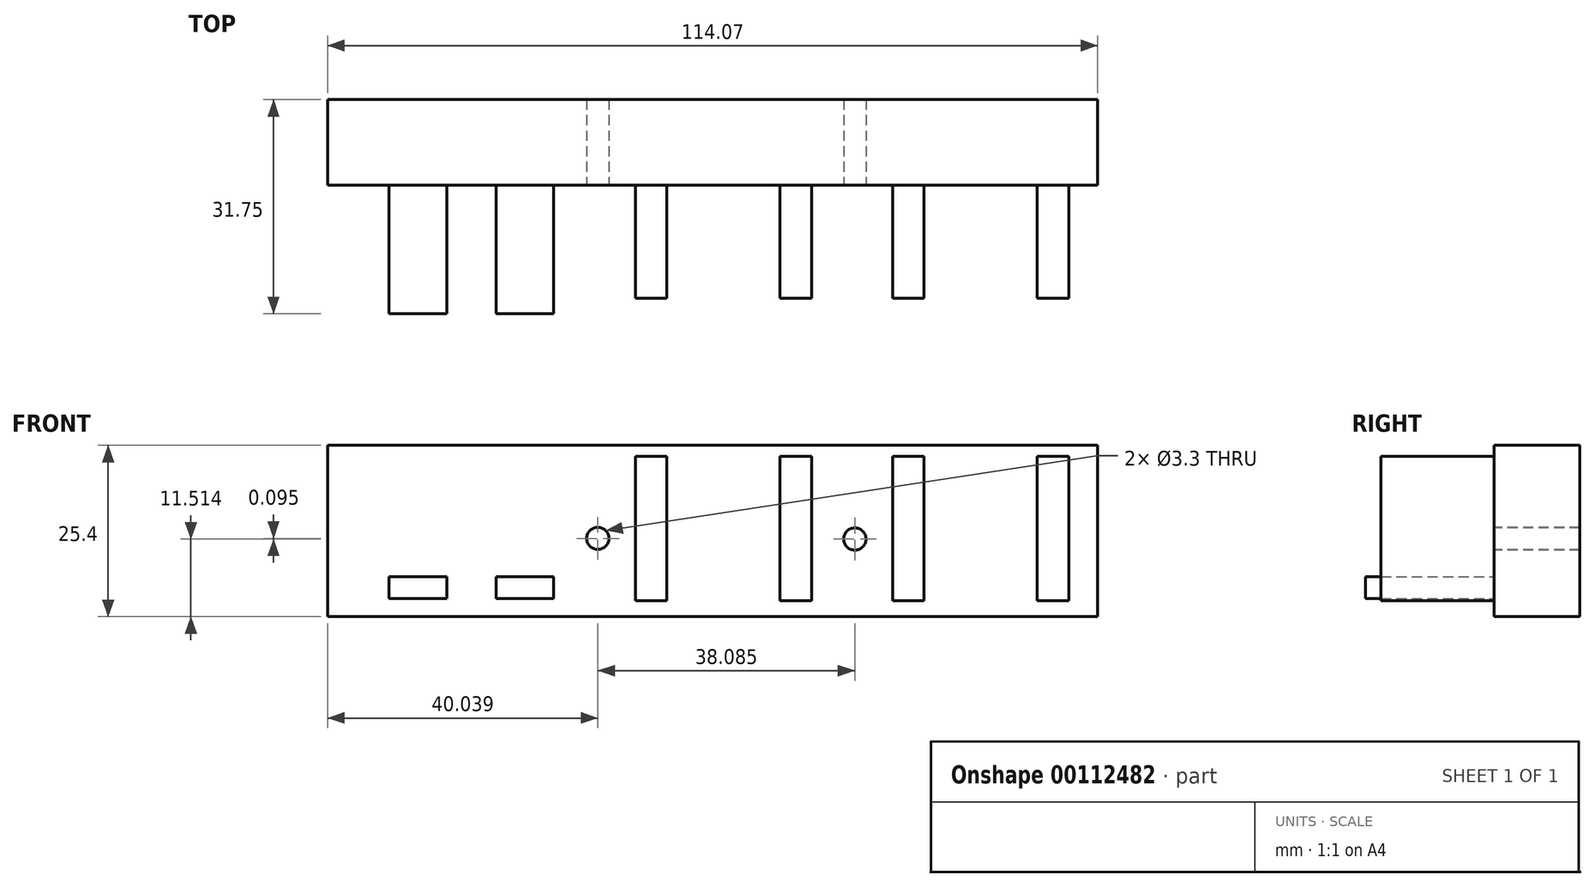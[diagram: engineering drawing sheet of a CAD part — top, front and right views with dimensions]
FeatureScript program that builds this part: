
annotation { "Feature Type Name" : "Feature", "Feature Type Description" : "" }
export const myFeature = defineFeature(function(context is Context, id is Id, definition is map)
    precondition{}
    {
        {
            var Q0;
            Q0=qCreatedBy(makeId("Front.planeOp"),FACE);
            var sketch = newSketch(context, id + "F0", { "sketchPlane" : qUnion([Q0])});
            skLineSegment(sketch, "E0", {"start": v(-72.64, 28.28) * mm, "end": v(54.36, 28.28) * mm});
            skLineSegment(sketch, "E1", {"start": v(54.36, 28.28) * mm, "end": v(54.36, 2.88) * mm});
            skLineSegment(sketch, "E2", {"start": v(54.36, 2.88) * mm, "end": v(-72.64, 2.88) * mm});
            skLineSegment(sketch, "E3", {"start": v(-72.64, 2.88) * mm, "end": v(-72.64, 28.28) * mm});
            skSolve(sketch);
        }
        {
            var Q0;
            Q0=makeQuery(id+"F0.imprint","IMPRINT",FACE,{"disambiguationData":[TD([[makeQuery(id+"F0.imprint","IMPRINT",EDGE,{"derivedFrom":sQuery(id+"F0.wireOp",EDGE,"E0")}),-1.0]])]});
            var sketch = newSketch(context, id + "F1", { "sketchPlane" : qUnion([Q0])});
            skLineSegment(sketch, "E4", {"start": v(50.08, 26.62) * mm, "end": v(50.08, 5.23) * mm});
            skLineSegment(sketch, "E5", {"start": v(50.08, 5.23) * mm, "end": v(45.41, 5.23) * mm});
            skLineSegment(sketch, "E6", {"start": v(45.41, 5.23) * mm, "end": v(45.41, 26.62) * mm});
            skLineSegment(sketch, "E7", {"start": v(45.41, 26.62) * mm, "end": v(50.08, 26.62) * mm});
            skLineSegment(sketch, "E8", {"start": v(45.41, 5.23) * mm, "end": v(28.65, 5.23) * mm, "construction": true});
            skLineSegment(sketch, "E9", {"start": v(28.65, 5.23) * mm, "end": v(28.65, 26.62) * mm});
            skLineSegment(sketch, "E10", {"start": v(28.65, 26.62) * mm, "end": v(23.98, 26.62) * mm});
            skLineSegment(sketch, "E11", {"start": v(23.98, 26.62) * mm, "end": v(23.98, 5.23) * mm});
            skLineSegment(sketch, "E12", {"start": v(23.98, 5.23) * mm, "end": v(28.65, 5.23) * mm});
            skLineSegment(sketch, "E13", {"start": v(11.99, 26.62) * mm, "end": v(11.99, 5.23) * mm});
            skLineSegment(sketch, "E14", {"start": v(11.99, 5.23) * mm, "end": v(7.32, 5.23) * mm});
            skLineSegment(sketch, "E15", {"start": v(7.32, 5.23) * mm, "end": v(7.32, 26.62) * mm});
            skLineSegment(sketch, "E16", {"start": v(7.32, 26.62) * mm, "end": v(11.99, 26.62) * mm});
            skLineSegment(sketch, "E17", {"start": v(7.32, 5.23) * mm, "end": v(-9.45, 5.23) * mm, "construction": true});
            skLineSegment(sketch, "E18", {"start": v(-9.45, 5.23) * mm, "end": v(-9.45, 26.62) * mm});
            skLineSegment(sketch, "E19", {"start": v(-9.45, 26.62) * mm, "end": v(-14.12, 26.62) * mm});
            skLineSegment(sketch, "E20", {"start": v(-14.12, 26.62) * mm, "end": v(-14.12, 5.23) * mm});
            skLineSegment(sketch, "E21", {"start": v(-14.12, 5.23) * mm, "end": v(-9.45, 5.23) * mm});
            skCircle(sketch, "E22", {"center": v(17.83, 15.92) * mm, "radius": 3.14 * mm});
            skPoint(sketch, "E22.centerSnap0", {"position": v(7.32, 15.92) * mm});
            skPoint(sketch, "E23.centerSnap0", {"position": v(-14.12, 15.92) * mm});
            skCircle(sketch, "E24", {"center": v(-23.8, 15.92) * mm, "radius": 3.31 * mm});
            skLineSegment(sketch, "E25", {"start": v(-35.22, 5.23) * mm, "end": v(-41.45, 5.23) * mm});
            skLineSegment(sketch, "E26", {"start": v(-41.45, 5.23) * mm, "end": v(-41.45, 8.48) * mm});
            skLineSegment(sketch, "E27", {"start": v(-41.45, 8.48) * mm, "end": v(-35.4, 8.48) * mm});
            skLineSegment(sketch, "E28", {"start": v(-35.4, 8.48) * mm, "end": v(-35.22, 5.23) * mm});
            skLineSegment(sketch, "E29", {"start": v(-47.33, 8.48) * mm, "end": v(-47.33, 5.23) * mm});
            skLineSegment(sketch, "E30", {"start": v(-47.33, 5.23) * mm, "end": v(-53.74, 5.23) * mm});
            skLineSegment(sketch, "E31", {"start": v(-53.74, 5.23) * mm, "end": v(-53.74, 8.48) * mm});
            skLineSegment(sketch, "E32", {"start": v(-53.74, 8.48) * mm, "end": v(-47.33, 8.48) * mm});
            skSolve(sketch);
        }
        {
            var Q0;
            Q0=makeQuery(id+"F0.imprint","IMPRINT",FACE,{"disambiguationData":[TD([[makeQuery(id+"F0.imprint","IMPRINT",EDGE,{"derivedFrom":sQuery(id+"F0.wireOp",EDGE,"E0")}),-1.0]])]});
            extrude(context, id + "F2", {"entities" : qUnion([Q0]), "oppositeDirection" : true, "depth" : 12.7 * mm});
        }
        {
            var Q0;
            Q0=makeQuery(id+"F1.imprint","IMPRINT",FACE,{"disambiguationData":[TD([[makeQuery(id+"F1.imprint","IMPRINT",EDGE,{"derivedFrom":sQuery(id+"F1.wireOp",EDGE,"E18")}),1.0]])]});
            var Q1;
            Q1=makeQuery(id+"F1.imprint","IMPRINT",FACE,{"disambiguationData":[TD([[makeQuery(id+"F1.imprint","IMPRINT",EDGE,{"derivedFrom":sQuery(id+"F1.wireOp",EDGE,"E13")}),-1.0]])]});
            var Q2;
            Q2=makeQuery(id+"F1.imprint","IMPRINT",FACE,{"disambiguationData":[TD([[makeQuery(id+"F1.imprint","IMPRINT",EDGE,{"derivedFrom":sQuery(id+"F1.wireOp",EDGE,"E9")}),1.0]])]});
            var Q3;
            Q3=makeQuery(id+"F1.imprint","IMPRINT",FACE,{"disambiguationData":[TD([[makeQuery(id+"F1.imprint","IMPRINT",EDGE,{"derivedFrom":sQuery(id+"F1.wireOp",EDGE,"E4")}),-1.0]])]});
            extrude(context, id + "F3", {"entities" : qUnion([Q0, Q1, Q2, Q3]), "operationType" : NewBodyOperationType.ADD, "depth" : 16.76 * mm});
        }
        {
            var Q0;
            Q0=makeQuery(id+"F2.opExtrude","CAP_FACE",FACE,{"disambiguationData":[OSD([sQuery(id+"F0.wireOp",EDGE,"E0"),sQuery(id+"F0.wireOp",EDGE,"E1"),sQuery(id+"F0.wireOp",EDGE,"E2"),sQuery(id+"F0.wireOp",EDGE,"E3")])],"isStart":true});
            var sketch = newSketch(context, id + "F4", { "sketchPlane" : qUnion([Q0])});
            skSolve(sketch);
        }
        {
            var Q0;
            Q0=makeQuery(id+"F4.imprint","IMPRINT",FACE,{"disambiguationData":[TD([[makeQuery(id+"F4.imprint","IMPRINT",EDGE,{"derivedFrom":makeQuery(id+"F2.opExtrude","CAP_EDGE",EDGE,{"disambiguationData":[OSD([sQuery(id+"F0.wireOp",EDGE,"E0")])],"isStart":true})}),-1.0]])]});
            var sketch = newSketch(context, id + "F5", { "sketchPlane" : qUnion([Q0])});
            skLineSegment(sketch, "E33", {"start": v(-26.2, 5.58) * mm, "end": v(-34.75, 5.58) * mm});
            skLineSegment(sketch, "E34", {"start": v(-34.75, 5.58) * mm, "end": v(-34.75, 8.81) * mm});
            skLineSegment(sketch, "E35", {"start": v(-34.75, 8.81) * mm, "end": v(-26.2, 8.81) * mm});
            skLineSegment(sketch, "E36", {"start": v(-26.2, 8.81) * mm, "end": v(-26.2, 5.58) * mm});
            skLineSegment(sketch, "E37", {"start": v(-42.01, 5.58) * mm, "end": v(-50.57, 5.58) * mm});
            skLineSegment(sketch, "E38", {"start": v(-50.57, 5.58) * mm, "end": v(-50.57, 8.81) * mm});
            skLineSegment(sketch, "E39", {"start": v(-50.57, 8.81) * mm, "end": v(-42.01, 8.81) * mm});
            skLineSegment(sketch, "E40", {"start": v(-42.01, 8.81) * mm, "end": v(-42.01, 5.58) * mm});
            skSolve(sketch);
        }
        {
            var Q0;
            Q0=makeQuery(id+"F5.imprint","IMPRINT",FACE,{"disambiguationData":[TD([[makeQuery(id+"F5.imprint","IMPRINT",EDGE,{"derivedFrom":sQuery(id+"F5.wireOp",EDGE,"E37")}),-1.0]])]});
            var Q1;
            Q1=makeQuery(id+"F5.imprint","IMPRINT",FACE,{"disambiguationData":[TD([[makeQuery(id+"F5.imprint","IMPRINT",EDGE,{"derivedFrom":sQuery(id+"F5.wireOp",EDGE,"E33")}),-1.0]])]});
            extrude(context, id + "F6", {"entities" : qUnion([Q0, Q1]), "operationType" : NewBodyOperationType.ADD, "depth" : 19.05 * mm});
        }
        {
            var Q0;
            Q0=makeQuery(id+"F4.imprint","IMPRINT",FACE,{"disambiguationData":[TD([[makeQuery(id+"F4.imprint","IMPRINT",EDGE,{"derivedFrom":makeQuery(id+"F2.opExtrude","CAP_EDGE",EDGE,{"disambiguationData":[OSD([sQuery(id+"F0.wireOp",EDGE,"E0")])],"isStart":true})}),-1.0]])]});
            var sketch = newSketch(context, id + "F7", { "sketchPlane" : qUnion([Q0])});
            skCircle(sketch, "E41", {"center": v(-19.67, 14.49) * mm, "radius": 1.65 * mm});
            skCircle(sketch, "E42", {"center": v(18.41, 14.4) * mm, "radius": 1.65 * mm});
            skSolve(sketch);
        }
        {
            var Q0;
            Q0=makeQuery(id+"F7.imprint","IMPRINT",FACE,{"disambiguationData":[TD([[makeQuery(id+"F7.imprint","IMPRINT",EDGE,{"derivedFrom":sQuery(id+"F7.wireOp",EDGE,"E41")}),-1.0]])]});
            var sketch = newSketch(context, id + "F8", { "sketchPlane" : qUnion([Q0])});
            skLineSegment(sketch, "E43", {"start": v(-59.71, 28.27) * mm, "end": v(-59.71, 2.89) * mm});
            skLineSegment(sketch, "E44", {"start": v(-59.71, 2.89) * mm, "end": v(-72.7, 2.89) * mm});
            skLineSegment(sketch, "E45", {"start": v(-72.7, 2.89) * mm, "end": v(-72.7, 28.34) * mm});
            skLineSegment(sketch, "E46", {"start": v(-72.7, 28.34) * mm, "end": v(-59.71, 28.27) * mm});
            skSolve(sketch);
        }
        {
            var Q0;
            Q0=makeQuery(id+"F7.imprint","IMPRINT",FACE,{"disambiguationData":[TD([[makeQuery(id+"F7.imprint","IMPRINT",EDGE,{"derivedFrom":sQuery(id+"F7.wireOp",EDGE,"E41")}),1.0]])]});
            var Q1;
            Q1=makeQuery(id+"F7.imprint","IMPRINT",FACE,{"disambiguationData":[TD([[makeQuery(id+"F7.imprint","IMPRINT",EDGE,{"derivedFrom":sQuery(id+"F7.wireOp",EDGE,"E42")}),1.0]])]});
            extrude(context, id + "F9", {"entities" : qUnion([Q0, Q1]), "operationType" : NewBodyOperationType.REMOVE, "endBound" : BoundingType.THROUGH_ALL, "oppositeDirection" : true, "depth" : 25.4 * mm});
        }
        {
            var Q0;
            {var subQ5=sQuery(id+"F8.wireOp",EDGE,"E43");Q0=makeQuery(id+"F8.imprint","IMPRINT",FACE,{"disambiguationData":[TD([[makeQuery(id+"F8.imprint","IMPRINT",EDGE,{"derivedFrom":subQ5}),-1.0]])]});}
            extrude(context, id + "F10", {"entities" : qUnion([Q0]), "operationType" : NewBodyOperationType.REMOVE, "oppositeDirection" : true, "depth" : 25.4 * mm});
        }
    });
